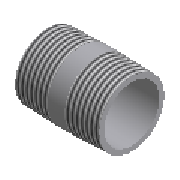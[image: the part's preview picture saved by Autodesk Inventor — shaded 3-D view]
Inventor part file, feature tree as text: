
AUTODESK INVENTOR PART (.ipt)
format: ipt  version: 2023.2 (Build 272271030, 271C)  size: 184,832 bytes
history: native  units: mm (DEFAULTED — no unit token found)
features: other x6, revolve x1, sketch x1
ambient origin geometry x8: Origin, YZ Plane, XZ Plane, XY Plane, X Axis, Y Axis, Z Axis, Center Point
bodies: Solid1 (feature_tree)
feature tree (8):
  revolve  "Revolution1"  [1 undecoded]
  other  "Work Point3"
  other  "Work Point4"
  other  "Work Axis1"
  other  "Work Point5"
  other  "Work Axis2"
  other  "Work Point6"
  sketch  "Sketch1"  dims[d12=90.0deg d1=0.312398mm d2=78.0mm d3=35.1mm d4=0.0mm d5=35.1mm d6=0.0mm d7=20.64mm d8=87.884mm d57=80.7mm d60=29.84mm d62=0.0mm]
note: 1 required parameter value undecoded (feature->parameter linkage not recoverable at this tier; creation-order binding heuristic only, values carry confidence <= 0.55)
